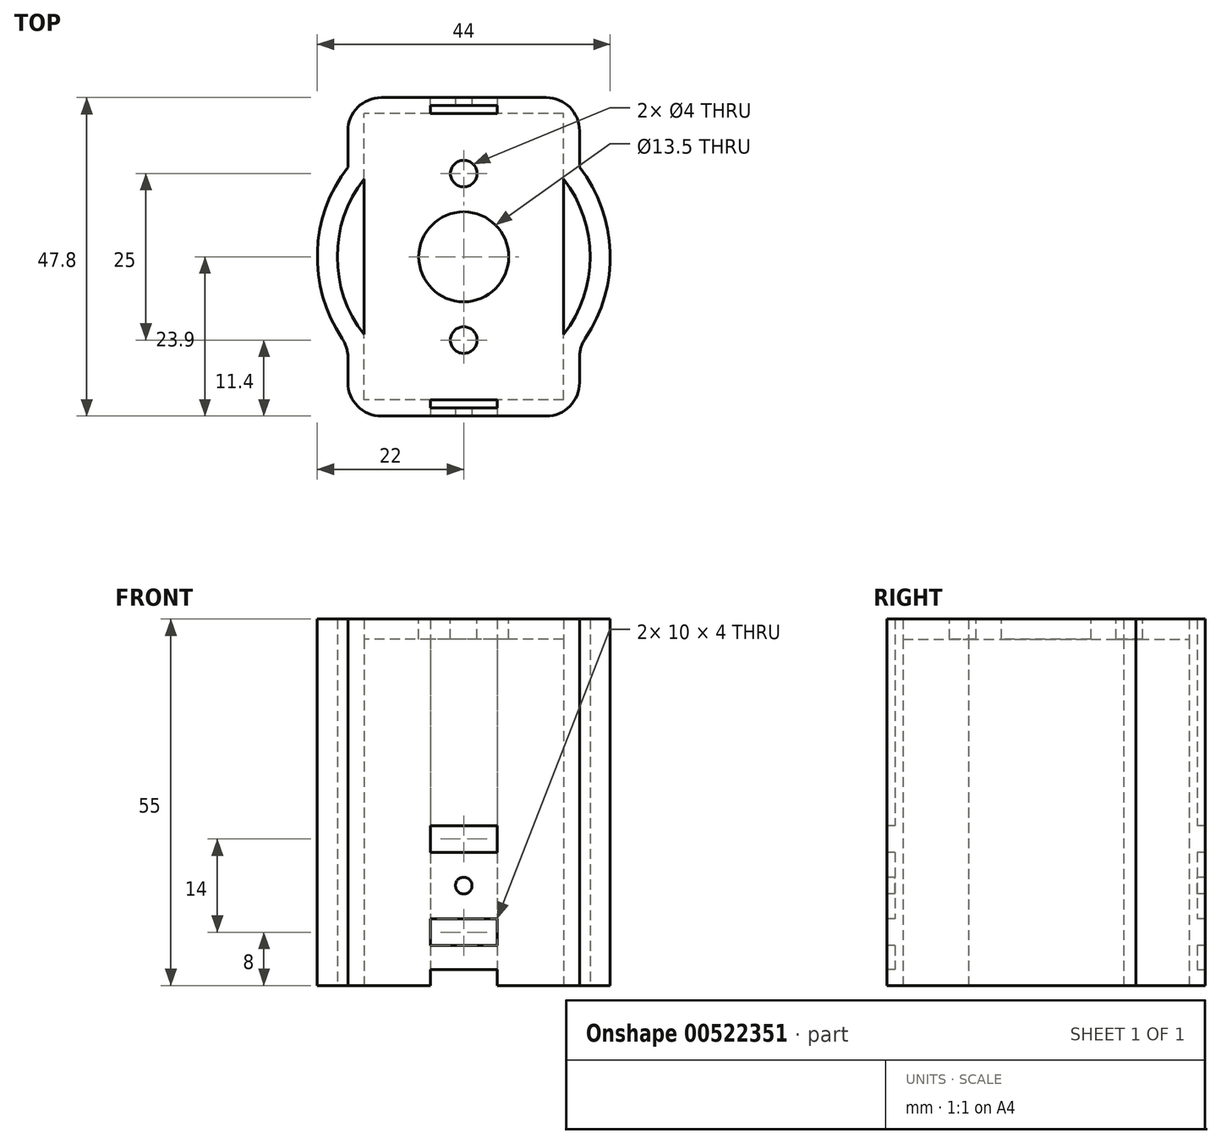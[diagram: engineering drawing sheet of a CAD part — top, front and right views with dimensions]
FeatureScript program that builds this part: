
annotation { "Feature Type Name" : "Feature", "Feature Type Description" : "" }
export const myFeature = defineFeature(function(context is Context, id is Id, definition is map)
    precondition{}
    {
        {
            var Q0;
            Q0=qCreatedBy(makeId("Top.planeOp"),FACE);
            var sketch = newSketch(context, id + "F0", { "sketchPlane" : qUnion([Q0])});
            skLineSegment(sketch, "E0.bottom", {"start": v(15, -21.5) * mm, "end": v(5, -21.5) * mm});
            skLineSegment(sketch, "E0.top", {"start": v(15, 21.5) * mm, "end": v(5, 21.5) * mm});
            skLineSegment(sketch, "E0.left", {"start": v(15, -21.5) * mm, "end": v(15, -11.66) * mm});
            skLineSegment(sketch, "E0.right", {"start": v(-15, -21.5) * mm, "end": v(-15, -11.66) * mm});
            skPoint(sketch, "E0.middle", {"position": v(0, 0) * mm});
            skLineSegment(sketch, "E1.bottom", {"start": v(5, -22.7) * mm, "end": v(-5, -22.7) * mm});
            skLineSegment(sketch, "E1.top", {"start": v(5, 22.7) * mm, "end": v(-5, 22.7) * mm});
            skLineSegment(sketch, "E2.bottom", {"start": v(17.4, -23.9) * mm, "end": v(-17.4, -23.9) * mm});
            skLineSegment(sketch, "E2.top", {"start": v(17.4, 23.9) * mm, "end": v(-17.4, 23.9) * mm});
            skLineSegment(sketch, "E2.left", {"start": v(17.4, -23.9) * mm, "end": v(17.4, -13.46) * mm});
            skLineSegment(sketch, "E2.right", {"start": v(-17.4, -23.9) * mm, "end": v(-17.4, -13.46) * mm});
            skLineSegment(sketch, "E3", {"start": v(-5, -21.5) * mm, "end": v(-5, -22.7) * mm});
            skLineSegment(sketch, "E4", {"start": v(5, -21.5) * mm, "end": v(5, -22.7) * mm});
            skLineSegment(sketch, "E5", {"start": v(0, 0) * mm, "end": v(0, -7.04) * mm, "construction": true});
            skLineSegment(sketch, "E6", {"start": v(0, 0) * mm, "end": v(8.38, 0) * mm, "construction": true});
            skLineSegment(sketch, "E7", {"start": v(-5, 22.7) * mm, "end": v(-5, 21.5) * mm});
            skLineSegment(sketch, "E8", {"start": v(5, 22.7) * mm, "end": v(5, 21.5) * mm});
            skLineSegment(sketch, "E9.trimOffspring", {"start": v(-5, 21.5) * mm, "end": v(-15, 21.5) * mm});
            skLineSegment(sketch, "E10.trimOffspring", {"start": v(-15, 11.66) * mm, "end": v(-15, 21.5) * mm});
            skLineSegment(sketch, "E11.trimOffspring", {"start": v(15, 11.66) * mm, "end": v(15, 21.5) * mm});
            skLineSegment(sketch, "E12.trimOffspring", {"start": v(-5, -21.5) * mm, "end": v(-15, -21.5) * mm});
            skPoint(sketch, "E13.orphan", {"position": v(-16.2, 22.7) * mm});
            skPoint(sketch, "E14.orphan", {"position": v(16.2, 22.7) * mm});
            skPoint(sketch, "E15.orphan", {"position": v(16.2, -22.7) * mm});
            skPoint(sketch, "E16.orphan", {"position": v(-16.2, -22.7) * mm});
            skLineSegment(sketch, "E17", {"start": v(5, 22.7) * mm, "end": v(5, 23.9) * mm});
            skLineSegment(sketch, "E18", {"start": v(-5, 22.7) * mm, "end": v(-5, 23.9) * mm});
            skLineSegment(sketch, "E19", {"start": v(-5, -22.7) * mm, "end": v(-5, -23.9) * mm});
            skLineSegment(sketch, "E20", {"start": v(5, -22.7) * mm, "end": v(5, -23.9) * mm});
            skArc(sketch, "E21", {"start": v(15, -11.66) * mm, "mid": v(19, 0) * mm, "end": v(15, 11.66) * mm});
            skArc(sketch, "E22.0", {"start": v(17.4, -13.46) * mm, "mid": v(22, 0) * mm, "end": v(17.4, 13.46) * mm});
            skLineSegment(sketch, "E23.trimOffspring", {"start": v(17.4, 13.46) * mm, "end": v(17.4, 23.9) * mm});
            skPoint(sketch, "E1.left.end.orphan", {"position": v(16.2, 5) * mm});
            skPoint(sketch, "E24.start.orphan", {"position": v(16.2, -5) * mm});
            skArc(sketch, "E25.trimOffspring", {"start": v(-15, 11.66) * mm, "mid": v(-19, 0) * mm, "end": v(-15, -11.66) * mm});
            skLineSegment(sketch, "E26.trimOffspring", {"start": v(-17.4, 13.46) * mm, "end": v(-17.4, 23.9) * mm});
            skPoint(sketch, "E27.start.orphan", {"position": v(-16.2, -5) * mm});
            skPoint(sketch, "E28.start.orphan", {"position": v(-16.2, 5) * mm});
            skArc(sketch, "E29.trimOffspring", {"start": v(-17.4, 13.46) * mm, "mid": v(-22, 0) * mm, "end": v(-17.4, -13.46) * mm});
            skSolve(sketch);
        }
        {
            var Q0;
            Q0=makeQuery(id+"F0.imprint","IMPRINT",FACE,{"disambiguationData":[TD([[makeQuery(id+"F0.imprint","IMPRINT",EDGE,{"derivedFrom":sQuery(id+"F0.wireOp",EDGE,"E0.bottom")}),1.0]])]});
            var Q1;
            Q1=makeQuery(id+"F0.imprint","IMPRINT",FACE,{"disambiguationData":[TD([[makeQuery(id+"F0.imprint","IMPRINT",EDGE,{"derivedFrom":sQuery(id+"F0.wireOp",EDGE,"E1.left")}),-1.0]])]});
            var Q2;
            Q2=makeQuery(id+"F0.imprint","IMPRINT",FACE,{"disambiguationData":[TD([[makeQuery(id+"F0.imprint","IMPRINT",EDGE,{"derivedFrom":sQuery(id+"F0.wireOp",EDGE,"E0.top")}),-1.0]])]});
            var Q3;
            Q3=makeQuery(id+"F0.imprint","IMPRINT",FACE,{"disambiguationData":[TD([[makeQuery(id+"F0.imprint","IMPRINT",EDGE,{"derivedFrom":sQuery(id+"F0.wireOp",EDGE,"E1.top")}),-1.0]])]});
            var Q4;
            Q4=makeQuery(id+"F0.imprint","IMPRINT",FACE,{"disambiguationData":[TD([[makeQuery(id+"F0.imprint","IMPRINT",EDGE,{"derivedFrom":sQuery(id+"F0.wireOp",EDGE,"i6ovlYtQ-0Uwt-BrMk-WHjt-l7IFheiTitFR")}),1.0]])]});
            var Q5;
            Q5=makeQuery(id+"F0.imprint","IMPRINT",FACE,{"disambiguationData":[TD([[makeQuery(id+"F0.imprint","IMPRINT",EDGE,{"derivedFrom":sQuery(id+"F0.wireOp",EDGE,"E0.right")}),1.0]])]});
            var Q6;
            Q6=makeQuery(id+"F0.imprint","IMPRINT",FACE,{"disambiguationData":[TD([[makeQuery(id+"F0.imprint","IMPRINT",EDGE,{"derivedFrom":sQuery(id+"F0.wireOp",EDGE,"E1.bottom")}),1.0]])]});
            var Q7;
            Q7=makeQuery(id+"F0.imprint","IMPRINT",FACE,{"disambiguationData":[TD([[makeQuery(id+"F0.imprint","IMPRINT",EDGE,{"derivedFrom":sQuery(id+"F0.wireOp",EDGE,"E1.right")}),1.0]])]});
            extrude(context, id + "F1", {"entities" : qUnion([Q0, Q1, Q2, Q3, Q4, Q5, Q6, Q7]), "depth" : 30 * mm, "offsetDistance" : 25 * mm});
        }
        {
            var Q0;
            Q0=makeQuery(id+"F1.opExtrude","SWEPT_FACE",FACE,{"disambiguationData":[OSD([sQuery(id+"F0.wireOp",EDGE,"E2.bottom")])]});
            var sketch = newSketch(context, id + "F2", { "sketchPlane" : qUnion([Q0])});
            skLineSegment(sketch, "E30.bottom", {"start": v(-5, 24) * mm, "end": v(5, 24) * mm});
            skLineSegment(sketch, "E30.top", {"start": v(-5, 20) * mm, "end": v(5, 20) * mm});
            skLineSegment(sketch, "E30.left", {"start": v(-5, 24) * mm, "end": v(-5, 20) * mm});
            skLineSegment(sketch, "E30.right", {"start": v(5, 24) * mm, "end": v(5, 20) * mm});
            skLineSegment(sketch, "E31", {"start": v(0, 30) * mm, "end": v(0, 0) * mm, "construction": true});
            skLineSegment(sketch, "E32.bottom", {"start": v(-5, 10) * mm, "end": v(5, 10) * mm});
            skLineSegment(sketch, "E32.top", {"start": v(-5, 6) * mm, "end": v(5, 6) * mm});
            skLineSegment(sketch, "E32.left", {"start": v(-5, 10) * mm, "end": v(-5, 6) * mm});
            skLineSegment(sketch, "E32.right", {"start": v(5, 10) * mm, "end": v(5, 6) * mm});
            skLineSegment(sketch, "E33", {"start": v(5, 10) * mm, "end": v(-5, 20) * mm, "construction": true});
            skLineSegment(sketch, "E34", {"start": v(5, 20) * mm, "end": v(-5, 10) * mm, "construction": true});
            skCircle(sketch, "E35", {"center": v(0, 15) * mm, "radius": 1.25 * mm});
            skSolve(sketch);
        }
        {
            var Q0;
            Q0=makeQuery(id+"F2.imprint","IMPRINT",FACE,{"disambiguationData":[TD([[makeQuery(id+"F2.imprint","IMPRINT",EDGE,{"derivedFrom":sQuery(id+"F2.wireOp",EDGE,"E30.bottom")}),-1.0]])]});
            var Q1;
            Q1=makeQuery(id+"F2.imprint","IMPRINT",FACE,{"disambiguationData":[TD([[makeQuery(id+"F2.imprint","IMPRINT",EDGE,{"derivedFrom":sQuery(id+"F2.wireOp",EDGE,"E32.bottom")}),-1.0]])]});
            var Q2;
            Q2=makeQuery(id+"F2.imprint","IMPRINT",FACE,{"disambiguationData":[TD([[makeQuery(id+"F2.imprint","IMPRINT",EDGE,{"derivedFrom":sQuery(id+"F2.wireOp",EDGE,"E35")}),1.0]])]});
            extrude(context, id + "F3", {"entities" : qUnion([Q0, Q1, Q2]), "operationType" : NewBodyOperationType.REMOVE, "endBound" : BoundingType.THROUGH_ALL, "oppositeDirection" : true, "depth" : 53.6 * mm, "offsetDistance" : 25 * mm});
        }
        {
            var Q0;
            Q0=makeQuery(id+"F0.imprint","IMPRINT",FACE,{"disambiguationData":[TD([[makeQuery(id+"F0.imprint","IMPRINT",EDGE,{"derivedFrom":sQuery(id+"F0.wireOp",EDGE,"E1.left")}),-1.0]])]});
            var Q1;
            Q1=makeQuery(id+"F0.imprint","IMPRINT",FACE,{"disambiguationData":[TD([[makeQuery(id+"F0.imprint","IMPRINT",EDGE,{"derivedFrom":sQuery(id+"F0.wireOp",EDGE,"E1.top")}),-1.0]])]});
            var Q2;
            Q2=makeQuery(id+"F0.imprint","IMPRINT",FACE,{"disambiguationData":[TD([[makeQuery(id+"F0.imprint","IMPRINT",EDGE,{"derivedFrom":sQuery(id+"F0.wireOp",EDGE,"E1.bottom")}),1.0]])]});
            var Q3;
            Q3=makeQuery(id+"F0.imprint","IMPRINT",FACE,{"disambiguationData":[TD([[makeQuery(id+"F0.imprint","IMPRINT",EDGE,{"derivedFrom":sQuery(id+"F0.wireOp",EDGE,"E1.right")}),1.0]])]});
            extrude(context, id + "F4", {"entities" : qUnion([Q0, Q1, Q2, Q3]), "operationType" : NewBodyOperationType.REMOVE, "depth" : 2.4 * mm, "offsetDistance" : 25 * mm});
        }
        {
            var Q0;
            Q0=makeQuery(id+"F1.opExtrude","SWEPT_EDGE",EDGE,{"disambiguationData":[OSD([sQuery(id+"F0.wireOp",EDGE,"E2.bottom"),sQuery(id+"F0.wireOp",EDGE,"E2.right")])]});
            var Q1;
            Q1=makeQuery(id+"F1.opExtrude","SWEPT_EDGE",EDGE,{"disambiguationData":[OSD([sQuery(id+"F0.wireOp",EDGE,"E2.top"),sQuery(id+"F0.wireOp",EDGE,"E2.right")])]});
            var Q2;
            Q2=makeQuery(id+"F1.opExtrude","SWEPT_EDGE",EDGE,{"disambiguationData":[OSD([sQuery(id+"F0.wireOp",EDGE,"E2.bottom"),sQuery(id+"F0.wireOp",EDGE,"E2.left")])]});
            var Q3;
            Q3=makeQuery(id+"F1.opExtrude","SWEPT_EDGE",EDGE,{"disambiguationData":[OSD([sQuery(id+"F0.wireOp",EDGE,"E2.top"),sQuery(id+"F0.wireOp",EDGE,"E2.left")])]});
            fillet(context, id + "F5", {"entities" : qUnion([Q0, Q1, Q2, Q3]), "radius" : 5 * mm, "tangentPropagation" : true, "allowEdgeOverflow" : false});
        }
        {
            var Q0;
            Q0=makeQuery(id+"F1.opExtrude","CAP_FACE",FACE,{"disambiguationData":[OSD([sQuery(id+"F0.wireOp",EDGE,"E0.bottom"),sQuery(id+"F0.wireOp",EDGE,"E0.top"),sQuery(id+"F0.wireOp",EDGE,"E0.left"),sQuery(id+"F0.wireOp",EDGE,"E0.right"),sQuery(id+"F0.wireOp",EDGE,"E1.bottom"),sQuery(id+"F0.wireOp",EDGE,"E1.top"),sQuery(id+"F0.wireOp",EDGE,"E2.bottom"),sQuery(id+"F0.wireOp",EDGE,"E2.top"),sQuery(id+"F0.wireOp",EDGE,"E2.left"),sQuery(id+"F0.wireOp",EDGE,"E2.right"),sQuery(id+"F0.wireOp",EDGE,"E3"),sQuery(id+"F0.wireOp",EDGE,"E4"),sQuery(id+"F0.wireOp",EDGE,"E7"),sQuery(id+"F0.wireOp",EDGE,"E8"),sQuery(id+"F0.wireOp",EDGE,"E9.trimOffspring"),sQuery(id+"F0.wireOp",EDGE,"E10.trimOffspring"),sQuery(id+"F0.wireOp",EDGE,"E11.trimOffspring"),sQuery(id+"F0.wireOp",EDGE,"E12.trimOffspring"),sQuery(id+"F0.wireOp",EDGE,"E21"),sQuery(id+"F0.wireOp",EDGE,"E22.0"),sQuery(id+"F0.wireOp",EDGE,"E23.trimOffspring"),sQuery(id+"F0.wireOp",EDGE,"E25.trimOffspring"),sQuery(id+"F0.wireOp",EDGE,"E26.trimOffspring"),sQuery(id+"F0.wireOp",EDGE,"E29.trimOffspring")])],"isStart":false});
            extrude(context, id + "F6", {"entities" : qUnion([Q0]), "operationType" : NewBodyOperationType.ADD, "depth" : 25 * mm, "offsetDistance" : 25 * mm});
        }
        {
            var Q0;
            Q0=makeQuery(id+"F6.opExtrude","CAP_FACE",FACE,{"disambiguationData":[OSD([sQuery(id+"F0.wireOp",EDGE,"E0.bottom"),sQuery(id+"F0.wireOp",EDGE,"E0.top"),sQuery(id+"F0.wireOp",EDGE,"E0.left"),sQuery(id+"F0.wireOp",EDGE,"E0.right"),sQuery(id+"F0.wireOp",EDGE,"E1.bottom"),sQuery(id+"F0.wireOp",EDGE,"E1.top"),sQuery(id+"F0.wireOp",EDGE,"E2.bottom"),sQuery(id+"F0.wireOp",EDGE,"E2.top"),sQuery(id+"F0.wireOp",EDGE,"E2.left"),sQuery(id+"F0.wireOp",EDGE,"E2.right"),sQuery(id+"F0.wireOp",EDGE,"E3"),sQuery(id+"F0.wireOp",EDGE,"E4"),sQuery(id+"F0.wireOp",EDGE,"E7"),sQuery(id+"F0.wireOp",EDGE,"E8"),sQuery(id+"F0.wireOp",EDGE,"E9.trimOffspring"),sQuery(id+"F0.wireOp",EDGE,"E10.trimOffspring"),sQuery(id+"F0.wireOp",EDGE,"E11.trimOffspring"),sQuery(id+"F0.wireOp",EDGE,"E12.trimOffspring"),sQuery(id+"F0.wireOp",EDGE,"E21"),sQuery(id+"F0.wireOp",EDGE,"E22.0"),sQuery(id+"F0.wireOp",EDGE,"E23.trimOffspring"),sQuery(id+"F0.wireOp",EDGE,"E25.trimOffspring"),sQuery(id+"F0.wireOp",EDGE,"E26.trimOffspring"),sQuery(id+"F0.wireOp",EDGE,"E29.trimOffspring")])],"isStart":false});
            var sketch = newSketch(context, id + "F7", { "sketchPlane" : qUnion([Q0])});
            skLineSegment(sketch, "E36.bottom", {"start": v(-15, -21.5) * mm, "end": v(15, -21.5) * mm});
            skLineSegment(sketch, "E36.top", {"start": v(-15, 21.5) * mm, "end": v(15, 21.5) * mm});
            skLineSegment(sketch, "E36.left", {"start": v(-15, -21.5) * mm, "end": v(-15, 21.5) * mm});
            skLineSegment(sketch, "E36.right", {"start": v(15, -21.5) * mm, "end": v(15, 21.5) * mm});
            skCircle(sketch, "E37", {"center": v(0, 0) * mm, "radius": 6.75 * mm});
            skCircle(sketch, "E38", {"center": v(0, -12.5) * mm, "radius": 2 * mm});
            skCircle(sketch, "E39", {"center": v(0, 12.5) * mm, "radius": 2 * mm});
            skSolve(sketch);
        }
        {
            var Q0;
            {var subQ1=sQuery(id+"F7.wireOp",EDGE,"E36.bottom");var subQ14=makeQuery(id+"F7.imprint","INTERSECT",VERTEX,{"derivedFrom":[makeQuery(id+"F6.opExtrude","CAP_EDGE",EDGE,{"disambiguationData":[OSD([sQuery(id+"F0.wireOp",EDGE,"E4")])],"isStart":false}),subQ1]});var subQ15=makeQuery(id+"F7.imprint","INTERSECT",VERTEX,{"derivedFrom":[makeQuery(id+"F6.opExtrude","CAP_EDGE",EDGE,{"disambiguationData":[OSD([sQuery(id+"F0.wireOp",EDGE,"E3")])],"isStart":false}),subQ1]});Q0=makeQuery(id+"F7.imprint","IMPRINT",FACE,{"disambiguationData":[TD([[makeQuery(id+"F7.imprint","IMPRINT",EDGE,{"disambiguationData":[TD([[subQ14,1.0],[subQ15,-1.0]])],"derivedFrom":subQ1}),1.0]])]});}
            extrude(context, id + "F8", {"entities" : qUnion([Q0]), "operationType" : NewBodyOperationType.ADD, "oppositeDirection" : true, "depth" : 3 * mm, "offsetDistance" : 25 * mm});
        }
    });
